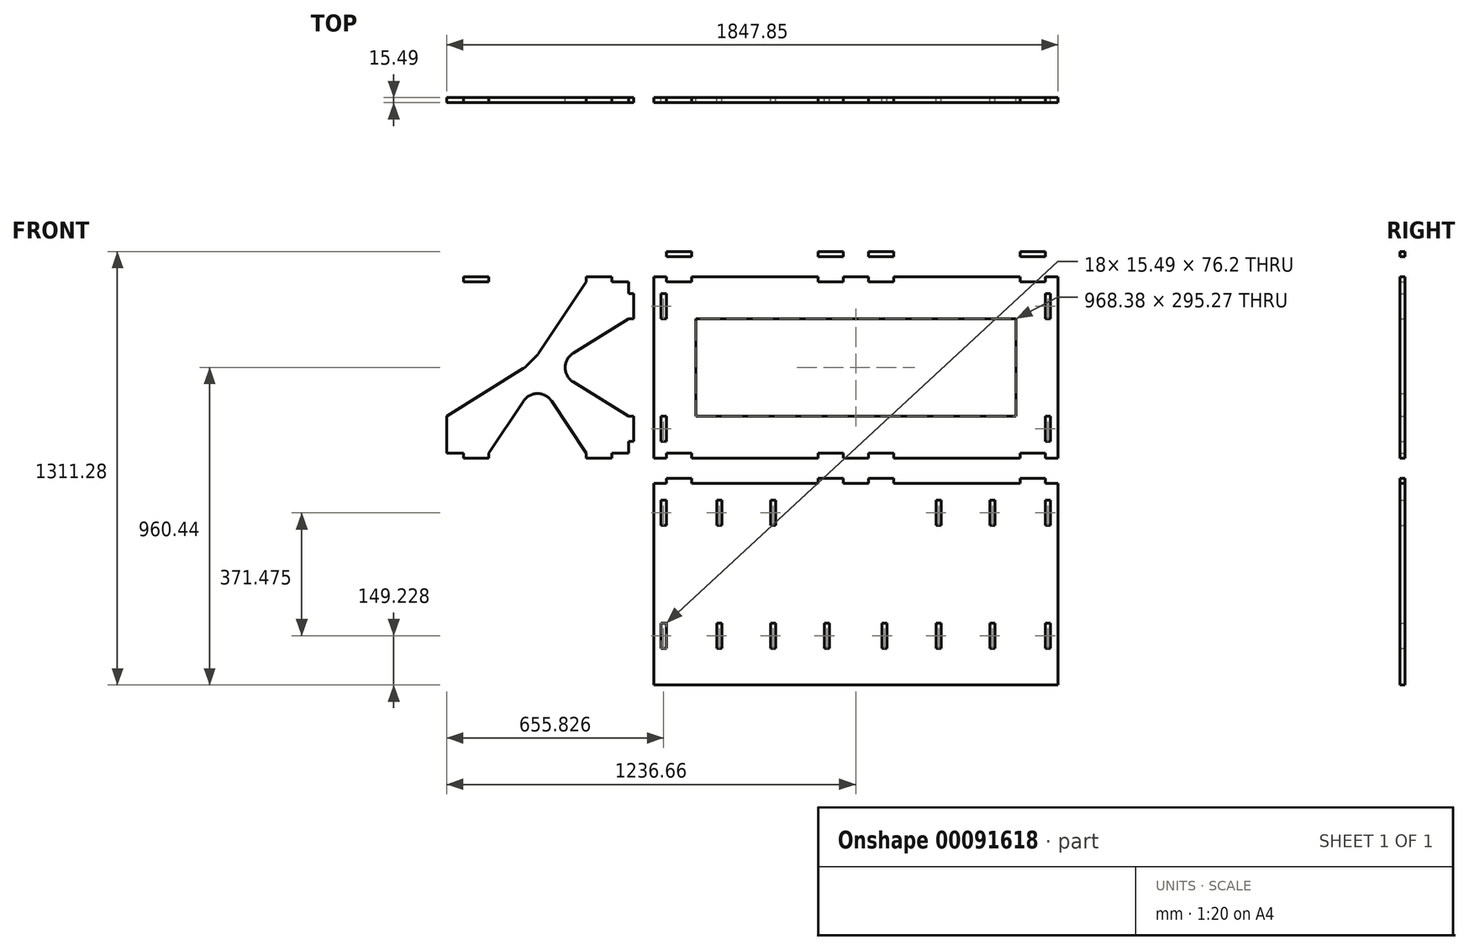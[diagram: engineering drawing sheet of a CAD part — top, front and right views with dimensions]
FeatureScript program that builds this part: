
annotation { "Feature Type Name" : "Feature", "Feature Type Description" : "" }
export const myFeature = defineFeature(function(context is Context, id is Id, definition is map)
    precondition{}
    {
        {
            var Q0;
            Q0=qCreatedBy(makeId("Front.planeOp"),FACE);
            var sketch = newSketch(context, id + "F0", { "sketchPlane" : qUnion([Q0])});
            skLineSegment(sketch, "E0.bottom", {"start": v(611.19, 274.64) * mm, "end": v(-611.19, 274.64) * mm});
            skLineSegment(sketch, "E0.top", {"start": v(611.19, -274.64) * mm, "end": v(-611.19, -274.64) * mm});
            skLineSegment(sketch, "E0.left", {"start": v(611.19, 274.64) * mm, "end": v(611.19, -274.64) * mm});
            skLineSegment(sketch, "E0.right", {"start": v(-611.19, 274.64) * mm, "end": v(-611.19, -274.64) * mm});
            skPoint(sketch, "E0.middle", {"position": v(0, 0) * mm});
            skLineSegment(sketch, "E1.bottom", {"start": v(-573.09, 274.64) * mm, "end": v(-496.89, 274.64) * mm});
            skLineSegment(sketch, "E1.top", {"start": v(-573.09, 258.89) * mm, "end": v(-496.89, 258.89) * mm});
            skLineSegment(sketch, "E1.left", {"start": v(-573.09, 274.64) * mm, "end": v(-573.09, 258.89) * mm});
            skLineSegment(sketch, "E1.right", {"start": v(-496.89, 274.64) * mm, "end": v(-496.89, 258.89) * mm});
            skLineSegment(sketch, "E2", {"start": v(0, 274.64) * mm, "end": v(0, -274.64) * mm, "construction": true});
            skLineSegment(sketch, "E3", {"start": v(-611.19, 0) * mm, "end": v(0, 0) * mm, "construction": true});
            skLineSegment(sketch, "E4", {"start": v(-305.6, -274.64) * mm, "end": v(-305.6, 274.64) * mm, "construction": true});
            skPoint(sketch, "E4.startSnap0", {"position": v(-305.6, 0) * mm});
            skLineSegment(sketch, "E5.MirrorCS", {"start": v(-114.3, 274.64) * mm, "end": v(-114.3, 258.89) * mm});
            skLineSegment(sketch, "E6.MirrorCS", {"start": v(-38.1, 274.64) * mm, "end": v(-38.1, 258.89) * mm});
            skLineSegment(sketch, "E7.MirrorCS", {"start": v(-38.1, 258.89) * mm, "end": v(-114.3, 258.89) * mm});
            skLineSegment(sketch, "E8.MirrorCS", {"start": v(-38.1, 274.64) * mm, "end": v(-114.3, 274.64) * mm});
            skLineSegment(sketch, "E9.MirrorCS", {"start": v(-38.1, -274.64) * mm, "end": v(-38.1, -258.89) * mm});
            skLineSegment(sketch, "E10.MirrorCS", {"start": v(-114.3, -274.64) * mm, "end": v(-114.3, -258.89) * mm});
            skLineSegment(sketch, "E11.MirrorCS", {"start": v(-496.89, -274.64) * mm, "end": v(-496.89, -258.89) * mm});
            skLineSegment(sketch, "E12.MirrorCS", {"start": v(-573.09, -274.64) * mm, "end": v(-573.09, -258.89) * mm});
            skLineSegment(sketch, "E13.MirrorCS", {"start": v(-38.1, -274.64) * mm, "end": v(-114.3, -274.64) * mm});
            skLineSegment(sketch, "E14.MirrorCS", {"start": v(-38.1, -258.89) * mm, "end": v(-114.3, -258.89) * mm});
            skLineSegment(sketch, "E15.MirrorCS", {"start": v(-573.09, -274.64) * mm, "end": v(-496.89, -274.64) * mm});
            skLineSegment(sketch, "E16.MirrorCS", {"start": v(-573.09, -258.89) * mm, "end": v(-496.89, -258.89) * mm});
            skLineSegment(sketch, "E17.MirrorCS", {"start": v(38.1, 274.64) * mm, "end": v(38.1, 258.89) * mm});
            skLineSegment(sketch, "E18.MirrorCS", {"start": v(114.3, 274.64) * mm, "end": v(114.3, 258.89) * mm});
            skLineSegment(sketch, "E19.MirrorCS", {"start": v(496.89, 274.64) * mm, "end": v(496.89, 258.89) * mm});
            skLineSegment(sketch, "E20.MirrorCS", {"start": v(573.09, 274.64) * mm, "end": v(573.09, 258.89) * mm});
            skLineSegment(sketch, "E21.MirrorCS", {"start": v(573.09, 274.64) * mm, "end": v(496.89, 274.64) * mm});
            skLineSegment(sketch, "E22.MirrorCS", {"start": v(573.09, 258.89) * mm, "end": v(496.89, 258.89) * mm});
            skLineSegment(sketch, "E23.MirrorCS", {"start": v(38.1, 274.64) * mm, "end": v(114.3, 274.64) * mm});
            skLineSegment(sketch, "E24.MirrorCS", {"start": v(38.1, 258.89) * mm, "end": v(114.3, 258.89) * mm});
            skLineSegment(sketch, "E25.MirrorCS", {"start": v(573.09, -274.64) * mm, "end": v(573.09, -258.89) * mm});
            skLineSegment(sketch, "E26.MirrorCS", {"start": v(496.89, -274.64) * mm, "end": v(496.89, -258.89) * mm});
            skLineSegment(sketch, "E27.MirrorCS", {"start": v(114.3, -274.64) * mm, "end": v(114.3, -258.89) * mm});
            skLineSegment(sketch, "E28.MirrorCS", {"start": v(38.1, -274.64) * mm, "end": v(38.1, -258.89) * mm});
            skLineSegment(sketch, "E29.MirrorCS", {"start": v(573.09, -258.89) * mm, "end": v(496.89, -258.89) * mm});
            skLineSegment(sketch, "E30.MirrorCS", {"start": v(573.09, -274.64) * mm, "end": v(496.89, -274.64) * mm});
            skLineSegment(sketch, "E31.MirrorCS", {"start": v(38.1, -274.64) * mm, "end": v(114.3, -274.64) * mm});
            skLineSegment(sketch, "E32.MirrorCS", {"start": v(38.1, -258.89) * mm, "end": v(114.3, -258.89) * mm});
            skLineSegment(sketch, "E33.bottom", {"start": v(-573.09, 223.84) * mm, "end": v(-588.58, 223.84) * mm});
            skLineSegment(sketch, "E33.top", {"start": v(-573.09, 147.64) * mm, "end": v(-588.58, 147.64) * mm});
            skLineSegment(sketch, "E33.left", {"start": v(-573.09, 223.84) * mm, "end": v(-573.09, 147.64) * mm});
            skLineSegment(sketch, "E33.right", {"start": v(-588.58, 223.84) * mm, "end": v(-588.58, 147.64) * mm});
            skLineSegment(sketch, "E34.MirrorCS", {"start": v(-573.09, -223.84) * mm, "end": v(-573.09, -147.64) * mm});
            skLineSegment(sketch, "E35.MirrorCS", {"start": v(-588.58, -223.84) * mm, "end": v(-588.58, -147.64) * mm});
            skLineSegment(sketch, "E36.MirrorCS", {"start": v(-573.09, -147.64) * mm, "end": v(-588.58, -147.64) * mm});
            skLineSegment(sketch, "E37.MirrorCS", {"start": v(-573.09, -223.84) * mm, "end": v(-588.58, -223.84) * mm});
            skLineSegment(sketch, "E38.MirrorCS", {"start": v(573.09, -223.84) * mm, "end": v(588.58, -223.84) * mm});
            skLineSegment(sketch, "E39.MirrorCS", {"start": v(573.09, -147.64) * mm, "end": v(588.58, -147.64) * mm});
            skLineSegment(sketch, "E40.MirrorCS", {"start": v(573.09, 223.84) * mm, "end": v(588.58, 223.84) * mm});
            skLineSegment(sketch, "E41.MirrorCS", {"start": v(573.09, 147.64) * mm, "end": v(588.58, 147.64) * mm});
            skLineSegment(sketch, "E42.MirrorCS", {"start": v(573.09, 223.84) * mm, "end": v(573.09, 147.64) * mm});
            skLineSegment(sketch, "E43.MirrorCS", {"start": v(588.58, 223.84) * mm, "end": v(588.58, 147.64) * mm});
            skLineSegment(sketch, "E44.MirrorCS", {"start": v(588.58, -223.84) * mm, "end": v(588.58, -147.64) * mm});
            skLineSegment(sketch, "E45.MirrorCS", {"start": v(573.09, -223.84) * mm, "end": v(573.09, -147.64) * mm});
            skLineSegment(sketch, "E46.bottom", {"start": v(-611.19, 350.84) * mm, "end": v(-3.17, 350.84) * mm});
            skLineSegment(sketch, "E46.top", {"start": v(-611.19, 960.44) * mm, "end": v(-3.18, 960.44) * mm});
            skLineSegment(sketch, "E46.left", {"start": v(-611.19, 350.84) * mm, "end": v(-611.19, 960.44) * mm});
            skLineSegment(sketch, "E46.right", {"start": v(-3.17, 350.84) * mm, "end": v(-3.18, 960.44) * mm});
            skLineSegment(sketch, "E47.bottom", {"start": v(611.19, 350.84) * mm, "end": v(0, 350.84) * mm});
            skLineSegment(sketch, "E47.top", {"start": v(611.19, 960.44) * mm, "end": v(0, 960.44) * mm});
            skLineSegment(sketch, "E47.left", {"start": v(611.19, 350.84) * mm, "end": v(611.19, 960.44) * mm});
            skLineSegment(sketch, "E47.right", {"start": v(0, 350.84) * mm, "end": v(0, 960.44) * mm});
            skLineSegment(sketch, "E48", {"start": v(-76.2, 258.89) * mm, "end": v(-76.2, 350.84) * mm, "construction": true});
            skLineSegment(sketch, "E49", {"start": v(-76.2, 304.86) * mm, "end": v(-114.3, 304.86) * mm, "construction": true});
            skPoint(sketch, "E49.endSnap0", {"position": v(-76.2, 304.86) * mm});
            skLineSegment(sketch, "E50.MirrorCS", {"start": v(496.89, 335.09) * mm, "end": v(496.89, 350.84) * mm});
            skLineSegment(sketch, "E51.MirrorCS", {"start": v(573.09, 335.09) * mm, "end": v(573.09, 350.84) * mm});
            skLineSegment(sketch, "E52.MirrorCS", {"start": v(114.3, 335.09) * mm, "end": v(114.3, 350.84) * mm});
            skLineSegment(sketch, "E53.MirrorCS", {"start": v(-573.09, 335.09) * mm, "end": v(-573.09, 350.84) * mm});
            skLineSegment(sketch, "E54.MirrorCS", {"start": v(-496.89, 335.09) * mm, "end": v(-496.89, 350.84) * mm});
            skLineSegment(sketch, "E55.MirrorCS", {"start": v(38.1, 335.09) * mm, "end": v(38.1, 350.84) * mm});
            skLineSegment(sketch, "E56.MirrorCS", {"start": v(-38.1, 335.09) * mm, "end": v(-38.1, 350.84) * mm});
            skLineSegment(sketch, "E57.MirrorCS", {"start": v(-114.3, 335.09) * mm, "end": v(-114.3, 350.84) * mm});
            skLineSegment(sketch, "E58.MirrorCS", {"start": v(-38.1, 335.09) * mm, "end": v(-114.3, 335.09) * mm});
            skLineSegment(sketch, "E59.MirrorCS", {"start": v(-38.1, 350.84) * mm, "end": v(-114.3, 350.84) * mm});
            skLineSegment(sketch, "E60.MirrorCS", {"start": v(-573.09, 335.09) * mm, "end": v(-496.89, 335.09) * mm});
            skLineSegment(sketch, "E61.MirrorCS", {"start": v(-573.09, 350.84) * mm, "end": v(-496.89, 350.84) * mm});
            skLineSegment(sketch, "E62.MirrorCS", {"start": v(573.09, 335.09) * mm, "end": v(496.89, 335.09) * mm});
            skLineSegment(sketch, "E63.MirrorCS", {"start": v(38.1, 335.09) * mm, "end": v(114.3, 335.09) * mm});
            skLineSegment(sketch, "E64.MirrorCS", {"start": v(573.09, 350.84) * mm, "end": v(496.89, 350.84) * mm});
            skLineSegment(sketch, "E65.MirrorCS", {"start": v(38.1, 350.84) * mm, "end": v(114.3, 350.84) * mm});
            skLineSegment(sketch, "E66", {"start": v(-611.19, 350.84) * mm, "end": v(-611.19, 274.64) * mm, "construction": true});
            skLineSegment(sketch, "E67", {"start": v(-611.19, 312.74) * mm, "end": v(-496.89, 312.74) * mm, "construction": true});
            skLineSegment(sketch, "E68.MirrorCS", {"start": v(-573.09, 773.11) * mm, "end": v(-588.58, 773.11) * mm});
            skLineSegment(sketch, "E69.MirrorCS", {"start": v(-573.09, 477.84) * mm, "end": v(-588.58, 477.84) * mm});
            skLineSegment(sketch, "E70.MirrorCS", {"start": v(-573.09, 401.64) * mm, "end": v(-588.58, 401.64) * mm});
            skLineSegment(sketch, "E71.MirrorCS", {"start": v(-573.09, 849.31) * mm, "end": v(-588.58, 849.31) * mm});
            skLineSegment(sketch, "E72.MirrorCS", {"start": v(-588.58, 401.64) * mm, "end": v(-588.58, 477.84) * mm});
            skLineSegment(sketch, "E73.MirrorCS", {"start": v(-573.09, 849.31) * mm, "end": v(-573.09, 773.11) * mm});
            skLineSegment(sketch, "E74.MirrorCS", {"start": v(-573.09, 401.64) * mm, "end": v(-573.09, 477.84) * mm});
            skLineSegment(sketch, "E75.MirrorCS", {"start": v(-588.58, 849.31) * mm, "end": v(-588.58, 773.11) * mm});
            skLineSegment(sketch, "E76.MirrorCS", {"start": v(573.09, 477.84) * mm, "end": v(588.58, 477.84) * mm});
            skLineSegment(sketch, "E77.MirrorCS", {"start": v(573.09, 401.64) * mm, "end": v(588.58, 401.64) * mm});
            skLineSegment(sketch, "E78.MirrorCS", {"start": v(573.09, 773.11) * mm, "end": v(588.58, 773.11) * mm});
            skLineSegment(sketch, "E79.MirrorCS", {"start": v(573.09, 849.31) * mm, "end": v(588.58, 849.31) * mm});
            skLineSegment(sketch, "E80.MirrorCS", {"start": v(573.09, 401.64) * mm, "end": v(573.09, 477.84) * mm});
            skLineSegment(sketch, "E81.MirrorCS", {"start": v(588.58, 849.31) * mm, "end": v(588.58, 773.11) * mm});
            skLineSegment(sketch, "E82.MirrorCS", {"start": v(573.09, 849.31) * mm, "end": v(573.09, 773.11) * mm});
            skLineSegment(sketch, "E83.MirrorCS", {"start": v(588.58, 401.64) * mm, "end": v(588.58, 477.84) * mm});
            skLineSegment(sketch, "E84.bottom", {"start": v(-687.39, 258.89) * mm, "end": v(-1236.66, 258.89) * mm});
            skLineSegment(sketch, "E84.top", {"start": v(-687.39, -258.89) * mm, "end": v(-1236.66, -258.89) * mm});
            skLineSegment(sketch, "E84.left", {"start": v(-687.39, 258.89) * mm, "end": v(-687.39, -258.89) * mm});
            skLineSegment(sketch, "E84.right", {"start": v(-1236.66, 258.89) * mm, "end": v(-1236.66, -258.89) * mm});
            skLineSegment(sketch, "E85", {"start": v(-738.19, 258.89) * mm, "end": v(-738.19, 274.38) * mm});
            skLineSegment(sketch, "E86", {"start": v(-738.19, 274.38) * mm, "end": v(-814.39, 274.38) * mm});
            skLineSegment(sketch, "E87", {"start": v(-814.39, 274.38) * mm, "end": v(-814.39, 258.89) * mm});
            skLineSegment(sketch, "E88", {"start": v(-687.39, 223.84) * mm, "end": v(-671.9, 223.84) * mm});
            skLineSegment(sketch, "E89", {"start": v(-671.9, 223.84) * mm, "end": v(-671.9, 147.64) * mm});
            skLineSegment(sketch, "E90", {"start": v(-671.9, 147.64) * mm, "end": v(-687.39, 147.64) * mm});
            skLineSegment(sketch, "E91.MirrorCS", {"start": v(-687.39, -223.84) * mm, "end": v(-671.9, -223.84) * mm});
            skLineSegment(sketch, "E92.MirrorCS", {"start": v(-671.9, -147.64) * mm, "end": v(-687.39, -147.64) * mm});
            skLineSegment(sketch, "E93.MirrorCS", {"start": v(-671.9, -223.84) * mm, "end": v(-671.9, -147.64) * mm});
            skLineSegment(sketch, "E94", {"start": v(-962.03, 258.89) * mm, "end": v(-962.03, -258.89) * mm, "construction": true});
            skLineSegment(sketch, "E95", {"start": v(-962.03, -38.1) * mm, "end": v(-1109.66, -258.89) * mm});
            skLineSegment(sketch, "E96", {"start": v(-962.03, -38.1) * mm, "end": v(-814.39, -258.89) * mm});
            skLineSegment(sketch, "E97.bottom", {"start": v(-1000.13, 38.1) * mm, "end": v(-923.93, 38.1) * mm, "construction": true});
            skLineSegment(sketch, "E97.top", {"start": v(-1000.13, -38.1) * mm, "end": v(-923.93, -38.1) * mm, "construction": true});
            skLineSegment(sketch, "E97.left", {"start": v(-1000.13, 38.1) * mm, "end": v(-1000.13, -38.1) * mm, "construction": true});
            skLineSegment(sketch, "E97.right", {"start": v(-923.93, 38.1) * mm, "end": v(-923.93, -38.1) * mm, "construction": true});
            skPoint(sketch, "E97.middle", {"position": v(-962.03, 0) * mm});
            skLineSegment(sketch, "E98", {"start": v(-1000.13, 0) * mm, "end": v(-1236.66, 147.64) * mm});
            skLineSegment(sketch, "E99", {"start": v(-1000.13, 0) * mm, "end": v(-1236.66, -147.64) * mm});
            skLineSegment(sketch, "E100", {"start": v(-962.03, 38.1) * mm, "end": v(-1109.66, 258.89) * mm});
            skLineSegment(sketch, "E101", {"start": v(-814.39, 258.89) * mm, "end": v(-962.03, 38.1) * mm});
            skLineSegment(sketch, "E102", {"start": v(-923.93, 0) * mm, "end": v(-687.39, 147.64) * mm});
            skLineSegment(sketch, "E103", {"start": v(-923.93, 0) * mm, "end": v(-687.39, -147.64) * mm});
            skLineSegment(sketch, "E104.MirrorCS", {"start": v(-573.09, -849.31) * mm, "end": v(-588.58, -849.31) * mm});
            skLineSegment(sketch, "E105.MirrorCS", {"start": v(-573.09, -773.11) * mm, "end": v(-588.58, -773.11) * mm});
            skLineSegment(sketch, "E106.MirrorCS", {"start": v(-573.09, -401.64) * mm, "end": v(-588.58, -401.64) * mm});
            skLineSegment(sketch, "E107.MirrorCS", {"start": v(-114.3, -335.09) * mm, "end": v(-114.3, -350.84) * mm});
            skLineSegment(sketch, "E108.MirrorCS", {"start": v(114.3, -335.09) * mm, "end": v(114.3, -350.84) * mm});
            skLineSegment(sketch, "E109.MirrorCS", {"start": v(-573.09, -477.84) * mm, "end": v(-588.58, -477.84) * mm});
            skLineSegment(sketch, "E110.MirrorCS", {"start": v(-573.09, -335.09) * mm, "end": v(-573.09, -350.84) * mm});
            skLineSegment(sketch, "E111.MirrorCS", {"start": v(-496.89, -335.09) * mm, "end": v(-496.89, -350.84) * mm});
            skLineSegment(sketch, "E112.MirrorCS", {"start": v(38.1, -335.09) * mm, "end": v(38.1, -350.84) * mm});
            skLineSegment(sketch, "E113.MirrorCS", {"start": v(-38.1, -335.09) * mm, "end": v(-38.1, -350.84) * mm});
            skLineSegment(sketch, "E114.MirrorCS", {"start": v(573.09, -477.84) * mm, "end": v(588.58, -477.84) * mm});
            skLineSegment(sketch, "E115.MirrorCS", {"start": v(573.09, -773.11) * mm, "end": v(588.58, -773.11) * mm});
            skLineSegment(sketch, "E116.MirrorCS", {"start": v(573.09, -401.64) * mm, "end": v(588.58, -401.64) * mm});
            skLineSegment(sketch, "E117.MirrorCS", {"start": v(573.09, -849.31) * mm, "end": v(588.58, -849.31) * mm});
            skLineSegment(sketch, "E118.MirrorCS", {"start": v(496.89, -335.09) * mm, "end": v(496.89, -350.84) * mm});
            skLineSegment(sketch, "E119.MirrorCS", {"start": v(573.09, -335.09) * mm, "end": v(573.09, -350.84) * mm});
            skLineSegment(sketch, "E120.MirrorCS", {"start": v(-38.1, -335.09) * mm, "end": v(-114.3, -335.09) * mm});
            skLineSegment(sketch, "E121.MirrorCS", {"start": v(-38.1, -350.84) * mm, "end": v(-114.3, -350.84) * mm});
            skLineSegment(sketch, "E122.MirrorCS", {"start": v(-588.58, -401.64) * mm, "end": v(-588.58, -477.84) * mm});
            skLineSegment(sketch, "E123.MirrorCS", {"start": v(-573.09, -849.31) * mm, "end": v(-573.09, -773.11) * mm});
            skLineSegment(sketch, "E124.MirrorCS", {"start": v(-573.09, -401.64) * mm, "end": v(-573.09, -477.84) * mm});
            skLineSegment(sketch, "E125.MirrorCS", {"start": v(-588.58, -849.31) * mm, "end": v(-588.58, -773.11) * mm});
            skLineSegment(sketch, "E126.MirrorCS", {"start": v(-573.09, -335.09) * mm, "end": v(-496.89, -335.09) * mm});
            skLineSegment(sketch, "E127.MirrorCS", {"start": v(573.09, -335.09) * mm, "end": v(496.89, -335.09) * mm});
            skLineSegment(sketch, "E128.MirrorCS", {"start": v(-573.09, -350.84) * mm, "end": v(-496.89, -350.84) * mm});
            skLineSegment(sketch, "E129.MirrorCS", {"start": v(38.1, -335.09) * mm, "end": v(114.3, -335.09) * mm});
            skLineSegment(sketch, "E130.MirrorCS", {"start": v(573.09, -350.84) * mm, "end": v(496.89, -350.84) * mm});
            skLineSegment(sketch, "E131.MirrorCS", {"start": v(573.09, -401.64) * mm, "end": v(573.09, -477.84) * mm});
            skLineSegment(sketch, "E132.MirrorCS", {"start": v(588.58, -849.31) * mm, "end": v(588.58, -773.11) * mm});
            skLineSegment(sketch, "E133.MirrorCS", {"start": v(38.1, -350.84) * mm, "end": v(114.3, -350.84) * mm});
            skLineSegment(sketch, "E134.MirrorCS", {"start": v(573.09, -849.31) * mm, "end": v(573.09, -773.11) * mm});
            skLineSegment(sketch, "E135.MirrorCS", {"start": v(588.58, -401.64) * mm, "end": v(588.58, -477.84) * mm});
            skLineSegment(sketch, "E136.MirrorCS", {"start": v(-611.19, -350.84) * mm, "end": v(-611.19, -960.44) * mm});
            skLineSegment(sketch, "E137.MirrorCS", {"start": v(611.19, -350.84) * mm, "end": v(611.19, -960.44) * mm});
            skLineSegment(sketch, "E138", {"start": v(-611.19, -350.84) * mm, "end": v(611.19, -350.84) * mm});
            skLineSegment(sketch, "E139", {"start": v(611.19, -960.44) * mm, "end": v(-611.19, -960.44) * mm});
            skLineSegment(sketch, "E140.MirrorCS", {"start": v(-738.19, -258.89) * mm, "end": v(-738.19, -274.38) * mm});
            skLineSegment(sketch, "E141.MirrorCS", {"start": v(-814.39, -274.38) * mm, "end": v(-814.39, -258.89) * mm});
            skLineSegment(sketch, "E142.MirrorCS", {"start": v(-738.19, -274.38) * mm, "end": v(-814.39, -274.38) * mm});
            skLineSegment(sketch, "E143", {"start": v(-496.89, 223.84) * mm, "end": v(-496.89, -223.84) * mm, "construction": true});
            skLineSegment(sketch, "E144", {"start": v(-738.19, -350.84) * mm, "end": v(-1185.86, -350.84) * mm});
            skPoint(sketch, "E145", {"position": v(-962.03, -350.84) * mm});
            skLineSegment(sketch, "E146.MirrorCS", {"start": v(-1109.66, -274.38) * mm, "end": v(-1109.66, -258.89) * mm});
            skLineSegment(sketch, "E147.MirrorCS", {"start": v(-1185.86, -274.38) * mm, "end": v(-1109.66, -274.38) * mm});
            skLineSegment(sketch, "E148.MirrorCS", {"start": v(-1185.86, -258.89) * mm, "end": v(-1185.86, -274.38) * mm});
            skLineSegment(sketch, "E149.MirrorCS", {"start": v(-1185.86, 258.89) * mm, "end": v(-1185.86, 274.38) * mm});
            skLineSegment(sketch, "E150.MirrorCS", {"start": v(-1185.86, 274.38) * mm, "end": v(-1109.66, 274.38) * mm});
            skLineSegment(sketch, "E151.MirrorCS", {"start": v(-1109.66, 274.38) * mm, "end": v(-1109.66, 258.89) * mm});
            skLineSegment(sketch, "E152", {"start": v(-333.98, 960.44) * mm, "end": v(-333.98, 350.84) * mm, "construction": true});
            skLineSegment(sketch, "E153.MirrorCS", {"start": v(-94.87, 477.84) * mm, "end": v(-79.37, 477.84) * mm});
            skLineSegment(sketch, "E154.MirrorCS", {"start": v(-94.87, 773.11) * mm, "end": v(-79.38, 773.11) * mm});
            skLineSegment(sketch, "E155.MirrorCS", {"start": v(-94.87, 401.64) * mm, "end": v(-79.38, 401.64) * mm});
            skLineSegment(sketch, "E156.MirrorCS", {"start": v(-94.87, 849.31) * mm, "end": v(-79.38, 849.31) * mm});
            skLineSegment(sketch, "E157.MirrorCS", {"start": v(-79.37, 401.64) * mm, "end": v(-79.37, 477.84) * mm});
            skLineSegment(sketch, "E158.MirrorCS", {"start": v(-94.87, 849.31) * mm, "end": v(-94.87, 773.11) * mm});
            skLineSegment(sketch, "E159.MirrorCS", {"start": v(-79.38, 849.31) * mm, "end": v(-79.38, 773.11) * mm});
            skLineSegment(sketch, "E160.MirrorCS", {"start": v(-94.87, 401.64) * mm, "end": v(-94.87, 477.84) * mm});
            skLineSegment(sketch, "E161.MirrorCS", {"start": v(94.87, 477.84) * mm, "end": v(79.37, 477.84) * mm});
            skLineSegment(sketch, "E162.MirrorCS", {"start": v(94.87, 773.11) * mm, "end": v(79.37, 773.11) * mm});
            skLineSegment(sketch, "E163.MirrorCS", {"start": v(94.87, 401.64) * mm, "end": v(79.37, 401.64) * mm});
            skLineSegment(sketch, "E164.MirrorCS", {"start": v(94.87, 849.31) * mm, "end": v(79.37, 849.31) * mm});
            skLineSegment(sketch, "E165.MirrorCS", {"start": v(79.37, 849.31) * mm, "end": v(79.37, 773.11) * mm});
            skLineSegment(sketch, "E166.MirrorCS", {"start": v(94.87, 401.64) * mm, "end": v(94.87, 477.84) * mm});
            skLineSegment(sketch, "E167.MirrorCS", {"start": v(94.87, 849.31) * mm, "end": v(94.87, 773.11) * mm});
            skLineSegment(sketch, "E168.MirrorCS", {"start": v(79.37, 401.64) * mm, "end": v(79.37, 477.84) * mm});
            skLineSegment(sketch, "E169.bottom", {"start": v(-420.69, 849.31) * mm, "end": v(-405.2, 849.31) * mm});
            skLineSegment(sketch, "E169.top", {"start": v(-420.69, 773.11) * mm, "end": v(-405.2, 773.11) * mm});
            skLineSegment(sketch, "E169.left", {"start": v(-420.69, 849.31) * mm, "end": v(-420.69, 773.11) * mm});
            skLineSegment(sketch, "E169.right", {"start": v(-405.2, 849.31) * mm, "end": v(-405.2, 773.11) * mm});
            skLineSegment(sketch, "E170", {"start": v(-405.2, 811.21) * mm, "end": v(-94.87, 811.21) * mm, "construction": true});
            skLineSegment(sketch, "E171.bottom", {"start": v(-257.78, 849.31) * mm, "end": v(-242.28, 849.31) * mm});
            skLineSegment(sketch, "E171.top", {"start": v(-257.78, 773.11) * mm, "end": v(-242.28, 773.11) * mm});
            skLineSegment(sketch, "E171.left", {"start": v(-257.78, 849.31) * mm, "end": v(-257.78, 773.11) * mm});
            skLineSegment(sketch, "E171.right", {"start": v(-242.28, 849.31) * mm, "end": v(-242.28, 773.11) * mm});
            skPoint(sketch, "E171.middle", {"position": v(-250.03, 811.21) * mm});
            skLineSegment(sketch, "E172.MirrorCS", {"start": v(257.78, 773.11) * mm, "end": v(242.28, 773.11) * mm});
            skLineSegment(sketch, "E173.MirrorCS", {"start": v(420.69, 773.11) * mm, "end": v(405.2, 773.11) * mm});
            skLineSegment(sketch, "E174.MirrorCS", {"start": v(257.78, 849.31) * mm, "end": v(242.28, 849.31) * mm});
            skLineSegment(sketch, "E175.MirrorCS", {"start": v(420.69, 849.31) * mm, "end": v(405.2, 849.31) * mm});
            skLineSegment(sketch, "E176.MirrorCS", {"start": v(420.69, 849.31) * mm, "end": v(420.69, 773.11) * mm});
            skLineSegment(sketch, "E177.MirrorCS", {"start": v(405.2, 849.31) * mm, "end": v(405.2, 773.11) * mm});
            skLineSegment(sketch, "E178.MirrorCS", {"start": v(257.78, 849.31) * mm, "end": v(257.78, 773.11) * mm});
            skLineSegment(sketch, "E179.MirrorCS", {"start": v(242.28, 849.31) * mm, "end": v(242.28, 773.11) * mm});
            skPoint(sketch, "E180.MirrorP", {"position": v(250.03, 811.21) * mm});
            skLineSegment(sketch, "E181.MirrorCS", {"start": v(-420.69, -773.11) * mm, "end": v(-405.2, -773.11) * mm});
            skLineSegment(sketch, "E182.MirrorCS", {"start": v(-257.78, -773.11) * mm, "end": v(-242.28, -773.11) * mm});
            skLineSegment(sketch, "E183.MirrorCS", {"start": v(-79.37, -849.31) * mm, "end": v(-79.37, -773.11) * mm});
            skLineSegment(sketch, "E184.MirrorCS", {"start": v(94.87, -773.11) * mm, "end": v(79.38, -773.11) * mm});
            skLineSegment(sketch, "E185.MirrorCS", {"start": v(420.69, -773.11) * mm, "end": v(405.2, -773.11) * mm});
            skLineSegment(sketch, "E186.MirrorCS", {"start": v(79.38, -849.31) * mm, "end": v(79.37, -773.11) * mm});
            skLineSegment(sketch, "E187.MirrorCS", {"start": v(420.69, -849.31) * mm, "end": v(420.69, -773.11) * mm});
            skLineSegment(sketch, "E188.MirrorCS", {"start": v(94.87, -849.31) * mm, "end": v(79.38, -849.31) * mm});
            skLineSegment(sketch, "E189.MirrorCS", {"start": v(-242.28, -849.31) * mm, "end": v(-242.28, -773.11) * mm});
            skLineSegment(sketch, "E190.MirrorCS", {"start": v(-257.78, -849.31) * mm, "end": v(-242.28, -849.31) * mm});
            skLineSegment(sketch, "E191.MirrorCS", {"start": v(257.78, -849.31) * mm, "end": v(242.28, -849.31) * mm});
            skLineSegment(sketch, "E192.MirrorCS", {"start": v(-94.87, -849.31) * mm, "end": v(-79.37, -849.31) * mm});
            skLineSegment(sketch, "E193.MirrorCS", {"start": v(257.78, -849.31) * mm, "end": v(257.78, -773.11) * mm});
            skLineSegment(sketch, "E194.MirrorCS", {"start": v(242.28, -849.31) * mm, "end": v(242.28, -773.11) * mm});
            skLineSegment(sketch, "E195.MirrorCS", {"start": v(-420.69, -849.31) * mm, "end": v(-405.2, -849.31) * mm});
            skLineSegment(sketch, "E196.MirrorCS", {"start": v(-94.87, -773.11) * mm, "end": v(-79.37, -773.11) * mm});
            skLineSegment(sketch, "E197.MirrorCS", {"start": v(257.78, -773.11) * mm, "end": v(242.28, -773.11) * mm});
            skLineSegment(sketch, "E198.MirrorCS", {"start": v(-405.2, -849.31) * mm, "end": v(-405.2, -773.11) * mm});
            skLineSegment(sketch, "E199.MirrorCS", {"start": v(-420.69, -849.31) * mm, "end": v(-420.69, -773.11) * mm});
            skLineSegment(sketch, "E200.MirrorCS", {"start": v(-94.87, -849.31) * mm, "end": v(-94.87, -773.11) * mm});
            skLineSegment(sketch, "E201.MirrorCS", {"start": v(-257.78, -849.31) * mm, "end": v(-257.78, -773.11) * mm});
            skLineSegment(sketch, "E202.MirrorCS", {"start": v(420.69, -849.31) * mm, "end": v(405.2, -849.31) * mm});
            skLineSegment(sketch, "E203.MirrorCS", {"start": v(405.2, -849.31) * mm, "end": v(405.2, -773.11) * mm});
            skLineSegment(sketch, "E204.MirrorCS", {"start": v(94.87, -849.31) * mm, "end": v(94.87, -773.11) * mm});
            skPoint(sketch, "E205.MirrorP", {"position": v(250.03, -811.21) * mm});
            skPoint(sketch, "E206.MirrorP", {"position": v(-250.03, -811.21) * mm});
            skLineSegment(sketch, "E207.MirrorCS", {"start": v(-405.2, -811.21) * mm, "end": v(-94.87, -811.21) * mm, "construction": true});
            skLineSegment(sketch, "E208", {"start": v(-333.98, 849.31) * mm, "end": v(-333.98, 401.64) * mm, "construction": true});
            skLineSegment(sketch, "E209", {"start": v(-333.98, 625.48) * mm, "end": v(-420.69, 625.48) * mm, "construction": true});
            skLineSegment(sketch, "E210.MirrorCS", {"start": v(-257.78, 401.64) * mm, "end": v(-242.28, 401.64) * mm});
            skLineSegment(sketch, "E211.MirrorCS", {"start": v(-257.78, 477.84) * mm, "end": v(-242.28, 477.84) * mm});
            skLineSegment(sketch, "E212.MirrorCS", {"start": v(-420.69, 477.84) * mm, "end": v(-405.2, 477.84) * mm});
            skLineSegment(sketch, "E213.MirrorCS", {"start": v(-420.69, 401.64) * mm, "end": v(-405.2, 401.64) * mm});
            skLineSegment(sketch, "E214.MirrorCS", {"start": v(-242.28, 401.64) * mm, "end": v(-242.28, 477.84) * mm});
            skLineSegment(sketch, "E215.MirrorCS", {"start": v(-257.78, 401.64) * mm, "end": v(-257.78, 477.84) * mm});
            skLineSegment(sketch, "E216.MirrorCS", {"start": v(-405.2, 401.64) * mm, "end": v(-405.2, 477.84) * mm});
            skPoint(sketch, "E217.MirrorP", {"position": v(-250.03, 439.74) * mm});
            skLineSegment(sketch, "E218.MirrorCS", {"start": v(-420.69, 401.64) * mm, "end": v(-420.69, 477.84) * mm});
            skLineSegment(sketch, "E219.MirrorCS", {"start": v(420.69, 401.64) * mm, "end": v(405.2, 401.64) * mm});
            skLineSegment(sketch, "E220.MirrorCS", {"start": v(257.78, 401.64) * mm, "end": v(242.28, 401.64) * mm});
            skLineSegment(sketch, "E221.MirrorCS", {"start": v(257.78, 477.84) * mm, "end": v(242.28, 477.84) * mm});
            skLineSegment(sketch, "E222.MirrorCS", {"start": v(420.69, 477.84) * mm, "end": v(405.2, 477.84) * mm});
            skLineSegment(sketch, "E223.MirrorCS", {"start": v(257.78, 401.64) * mm, "end": v(257.78, 477.84) * mm});
            skLineSegment(sketch, "E224.MirrorCS", {"start": v(242.28, 401.64) * mm, "end": v(242.28, 477.84) * mm});
            skPoint(sketch, "E225.MirrorP", {"position": v(250.03, 439.74) * mm});
            skLineSegment(sketch, "E226.MirrorCS", {"start": v(420.69, 401.64) * mm, "end": v(420.69, 477.84) * mm});
            skLineSegment(sketch, "E227.MirrorCS", {"start": v(405.2, 401.64) * mm, "end": v(405.2, 477.84) * mm});
            skLineSegment(sketch, "E228.MirrorCS", {"start": v(-257.78, -477.84) * mm, "end": v(-242.28, -477.84) * mm});
            skLineSegment(sketch, "E229.MirrorCS", {"start": v(-420.69, -477.84) * mm, "end": v(-405.2, -477.84) * mm});
            skLineSegment(sketch, "E230.MirrorCS", {"start": v(-257.78, -401.64) * mm, "end": v(-242.28, -401.64) * mm});
            skLineSegment(sketch, "E231.MirrorCS", {"start": v(-420.69, -401.64) * mm, "end": v(-405.2, -401.64) * mm});
            skLineSegment(sketch, "E232.MirrorCS", {"start": v(-242.28, -401.64) * mm, "end": v(-242.28, -477.84) * mm});
            skPoint(sketch, "E233.MirrorP", {"position": v(-250.03, -439.74) * mm});
            skLineSegment(sketch, "E234.MirrorCS", {"start": v(-420.69, -401.64) * mm, "end": v(-420.69, -477.84) * mm});
            skLineSegment(sketch, "E235.MirrorCS", {"start": v(-257.78, -401.64) * mm, "end": v(-257.78, -477.84) * mm});
            skLineSegment(sketch, "E236.MirrorCS", {"start": v(-405.2, -401.64) * mm, "end": v(-405.2, -477.84) * mm});
            skLineSegment(sketch, "E237.MirrorCS", {"start": v(420.69, -401.64) * mm, "end": v(405.2, -401.64) * mm});
            skLineSegment(sketch, "E238.MirrorCS", {"start": v(257.78, -401.64) * mm, "end": v(242.28, -401.64) * mm});
            skLineSegment(sketch, "E239.MirrorCS", {"start": v(257.78, -477.84) * mm, "end": v(242.28, -477.84) * mm});
            skLineSegment(sketch, "E240.MirrorCS", {"start": v(420.69, -477.84) * mm, "end": v(405.2, -477.84) * mm});
            skLineSegment(sketch, "E241.MirrorCS", {"start": v(257.78, -401.64) * mm, "end": v(257.78, -477.84) * mm});
            skLineSegment(sketch, "E242.MirrorCS", {"start": v(242.28, -401.64) * mm, "end": v(242.28, -477.84) * mm});
            skPoint(sketch, "E243.MirrorP", {"position": v(250.03, -439.74) * mm});
            skLineSegment(sketch, "E244.MirrorCS", {"start": v(405.2, -401.64) * mm, "end": v(405.2, -477.84) * mm});
            skLineSegment(sketch, "E245.MirrorCS", {"start": v(420.69, -401.64) * mm, "end": v(420.69, -477.84) * mm});
            skLineSegment(sketch, "E246.bottom", {"start": v(-484.19, 147.64) * mm, "end": v(484.19, 147.64) * mm});
            skLineSegment(sketch, "E246.top", {"start": v(-484.19, -147.64) * mm, "end": v(484.19, -147.64) * mm});
            skLineSegment(sketch, "E246.left", {"start": v(-484.19, 147.64) * mm, "end": v(-484.19, -147.64) * mm});
            skLineSegment(sketch, "E246.right", {"start": v(484.19, 147.64) * mm, "end": v(484.19, -147.64) * mm});
            skLineSegment(sketch, "E247.0", {"start": v(-611.19, 579.44) * mm, "end": v(-3.17, 579.44) * mm});
            skLineSegment(sketch, "E248.0", {"start": v(611.19, 579.44) * mm, "end": v(0, 579.44) * mm});
            skLineSegment(sketch, "E249", {"start": v(-1000.13, 0) * mm, "end": v(-962.03, 38.1) * mm});
            skSolve(sketch);
        }
        {
            var Q0;
            Q0=makeQuery(id+"F0.imprint","IMPRINT",FACE,{"disambiguationData":[TD([[makeQuery(id+"F0.imprint","IMPRINT",EDGE,{"derivedFrom":sQuery(id+"F0.wireOp",EDGE,"92eabbe3-f8f1-4d0b-bcb1-c722cdc1d4602.MirrorCS")}),-1.0]])]});
            var Q1;
            {var subQ0=sQuery(id+"F0.wireOp",EDGE,"92eabbe3-f8f1-4d0b-bcb1-c722cdc1d4600.MirrorCS");Q1=makeQuery(id+"F0.imprint","IMPRINT",FACE,{"disambiguationData":[TD([[makeQuery(id+"F0.imprint","IMPRINT",EDGE,{"derivedFrom":subQ0}),1.0]])]});}
            var Q2;
            {var subQ0=sQuery(id+"F0.wireOp",EDGE,"E85");Q2=makeQuery(id+"F0.imprint","IMPRINT",FACE,{"disambiguationData":[TD([[makeQuery(id+"F0.imprint","IMPRINT",EDGE,{"derivedFrom":subQ0}),1.0]])]});}
            var Q3;
            {var subQ0=sQuery(id+"F0.wireOp",EDGE,"E88");Q3=makeQuery(id+"F0.imprint","IMPRINT",FACE,{"disambiguationData":[TD([[makeQuery(id+"F0.imprint","IMPRINT",EDGE,{"derivedFrom":subQ0}),-1.0]])]});}
            var Q4;
            {var subQ0=sQuery(id+"F0.wireOp",EDGE,"E91.MirrorCS");Q4=makeQuery(id+"F0.imprint","IMPRINT",FACE,{"disambiguationData":[TD([[makeQuery(id+"F0.imprint","IMPRINT",EDGE,{"derivedFrom":subQ0}),1.0]])]});}
            var Q5;
            Q5=makeQuery(id+"F0.imprint","IMPRINT",FACE,{"disambiguationData":[TD([[makeQuery(id+"F0.imprint","IMPRINT",EDGE,{"derivedFrom":sQuery(id+"F0.wireOp",EDGE,"58aca8fd-671b-425e-b90f-f2314bb2d9823.MirrorCS")}),-1.0]])]});
            var Q6;
            {var subQ0=sQuery(id+"F0.wireOp",EDGE,"5484c05e-e100-47fc-b072-6ca6ee2ab5f80.MirrorCS");Q6=makeQuery(id+"F0.imprint","IMPRINT",FACE,{"disambiguationData":[TD([[makeQuery(id+"F0.imprint","IMPRINT",EDGE,{"derivedFrom":subQ0}),1.0]])]});}
            var Q7;
            {var subQ0=sQuery(id+"F0.wireOp",EDGE,"5484c05e-e100-47fc-b072-6ca6ee2ab5f82.MirrorCS");Q7=makeQuery(id+"F0.imprint","IMPRINT",FACE,{"disambiguationData":[TD([[makeQuery(id+"F0.imprint","IMPRINT",EDGE,{"derivedFrom":subQ0}),-1.0]])]});}
            var Q8;
            Q8=makeQuery(id+"F0.imprint","IMPRINT",FACE,{"disambiguationData":[TD([[makeQuery(id+"F0.imprint","IMPRINT",EDGE,{"derivedFrom":sQuery(id+"F0.wireOp",EDGE,"E53.MirrorCS")}),-1.0]])]});
            var Q9;
            Q9=makeQuery(id+"F0.imprint","IMPRINT",FACE,{"disambiguationData":[TD([[makeQuery(id+"F0.imprint","IMPRINT",EDGE,{"derivedFrom":sQuery(id+"F0.wireOp",EDGE,"E56.MirrorCS")}),1.0]])]});
            var Q10;
            Q10=makeQuery(id+"F0.imprint","IMPRINT",FACE,{"disambiguationData":[TD([[makeQuery(id+"F0.imprint","IMPRINT",EDGE,{"derivedFrom":sQuery(id+"F0.wireOp",EDGE,"E52.MirrorCS")}),1.0]])]});
            var Q11;
            Q11=makeQuery(id+"F0.imprint","IMPRINT",FACE,{"disambiguationData":[TD([[makeQuery(id+"F0.imprint","IMPRINT",EDGE,{"derivedFrom":sQuery(id+"F0.wireOp",EDGE,"E50.MirrorCS")}),-1.0]])]});
            var Q12;
            Q12=makeQuery(id+"F0.imprint","IMPRINT",FACE,{"disambiguationData":[TD([[makeQuery(id+"F0.imprint","IMPRINT",EDGE,{"derivedFrom":sQuery(id+"F0.wireOp",EDGE,"E104.MirrorCS")}),1.0]])]});
            var Q13;
            {var subQ0=sQuery(id+"F0.wireOp",EDGE,"E110.MirrorCS");Q13=makeQuery(id+"F0.imprint","IMPRINT",FACE,{"disambiguationData":[TD([[makeQuery(id+"F0.imprint","IMPRINT",EDGE,{"derivedFrom":subQ0}),1.0]])]});}
            var Q14;
            {var subQ0=sQuery(id+"F0.wireOp",EDGE,"E118.MirrorCS");Q14=makeQuery(id+"F0.imprint","IMPRINT",FACE,{"disambiguationData":[TD([[makeQuery(id+"F0.imprint","IMPRINT",EDGE,{"derivedFrom":subQ0}),1.0]])]});}
            var Q15;
            {var subQ0=sQuery(id+"F0.wireOp",EDGE,"E107.MirrorCS");Q15=makeQuery(id+"F0.imprint","IMPRINT",FACE,{"disambiguationData":[TD([[makeQuery(id+"F0.imprint","IMPRINT",EDGE,{"derivedFrom":subQ0}),1.0]])]});}
            var Q16;
            {var subQ0=sQuery(id+"F0.wireOp",EDGE,"E108.MirrorCS");Q16=makeQuery(id+"F0.imprint","IMPRINT",FACE,{"disambiguationData":[TD([[makeQuery(id+"F0.imprint","IMPRINT",EDGE,{"derivedFrom":subQ0}),-1.0]])]});}
            var Q17;
            {var subQ2=sQuery(id+"F0.wireOp",EDGE,"E95");Q17=makeQuery(id+"F0.imprint","IMPRINT",FACE,{"disambiguationData":[TD([[makeQuery(id+"F0.imprint","IMPRINT",EDGE,{"derivedFrom":subQ2}),-1.0]])]});}
            var Q18;
            {var subQ1=sQuery(id+"F0.wireOp",EDGE,"E0.left");Q18=makeQuery(id+"F0.imprint","IMPRINT",FACE,{"disambiguationData":[TD([[makeQuery(id+"F0.imprint","IMPRINT",EDGE,{"derivedFrom":subQ1}),-1.0]])]});}
            var Q19;
            {var subQ2=sQuery(id+"F0.wireOp",EDGE,"E149.MirrorCS");Q19=makeQuery(id+"F0.imprint","IMPRINT",FACE,{"disambiguationData":[TD([[makeQuery(id+"F0.imprint","IMPRINT",EDGE,{"derivedFrom":subQ2}),-1.0]])]});}
            var Q20;
            {var subQ0=sQuery(id+"F0.wireOp",EDGE,"E146.MirrorCS");Q20=makeQuery(id+"F0.imprint","IMPRINT",FACE,{"disambiguationData":[TD([[makeQuery(id+"F0.imprint","IMPRINT",EDGE,{"derivedFrom":subQ0}),1.0]])]});}
            var Q21;
            {var subQ3=sQuery(id+"F0.wireOp",EDGE,"E59.MirrorCS");Q21=makeQuery(id+"F0.imprint","IMPRINT",FACE,{"disambiguationData":[TD([[makeQuery(id+"F0.imprint","IMPRINT",EDGE,{"derivedFrom":subQ3}),-1.0]])]});}
            var Q22;
            {var subQ7=sQuery(id+"F0.wireOp",EDGE,"E64.MirrorCS");Q22=makeQuery(id+"F0.imprint","IMPRINT",FACE,{"disambiguationData":[TD([[makeQuery(id+"F0.imprint","IMPRINT",EDGE,{"derivedFrom":subQ7}),-1.0]])]});}
            var Q23;
            {var subQ2=sQuery(id+"F0.wireOp",EDGE,"E140.MirrorCS");Q23=makeQuery(id+"F0.imprint","IMPRINT",FACE,{"disambiguationData":[TD([[makeQuery(id+"F0.imprint","IMPRINT",EDGE,{"derivedFrom":subQ2}),-1.0]])]});}
            extrude(context, id + "F1", {"entities" : qUnion([Q0, Q1, Q2, Q3, Q4, Q5, Q6, Q7, Q8, Q9, Q10, Q11, Q12, Q13, Q14, Q15, Q16, Q17, Q18, Q19, Q20, Q21, Q22, Q23]), "depth" : 15.5 * mm});
        }
        {
            var Q0;
            Q0=makeQuery(id+"F1.opExtrude","SWEPT_EDGE",EDGE,{"disambiguationData":[OSD([sQuery(id+"F0.wireOp",EDGE,"E98"),sQuery(id+"F0.wireOp",EDGE,"E99")])]});
            var Q1;
            Q1=makeQuery(id+"F1.opExtrude","SWEPT_EDGE",EDGE,{"disambiguationData":[OSD([sQuery(id+"F0.wireOp",EDGE,"E100"),sQuery(id+"F0.wireOp",EDGE,"E101")])]});
            var Q2;
            Q2=makeQuery(id+"F1.opExtrude","SWEPT_EDGE",EDGE,{"disambiguationData":[OSD([sQuery(id+"F0.wireOp",EDGE,"E102"),sQuery(id+"F0.wireOp",EDGE,"E103")])]});
            var Q3;
            Q3=makeQuery(id+"F1.opExtrude","SWEPT_EDGE",EDGE,{"disambiguationData":[OSD([sQuery(id+"F0.wireOp",EDGE,"E95"),sQuery(id+"F0.wireOp",EDGE,"E96")])]});
            fillet(context, id + "F2", {"entities" : qUnion([Q0, Q1, Q2, Q3]), "radius" : 50.8 * mm, "tangentPropagation" : true, "allowEdgeOverflow" : false});
        }
    });
